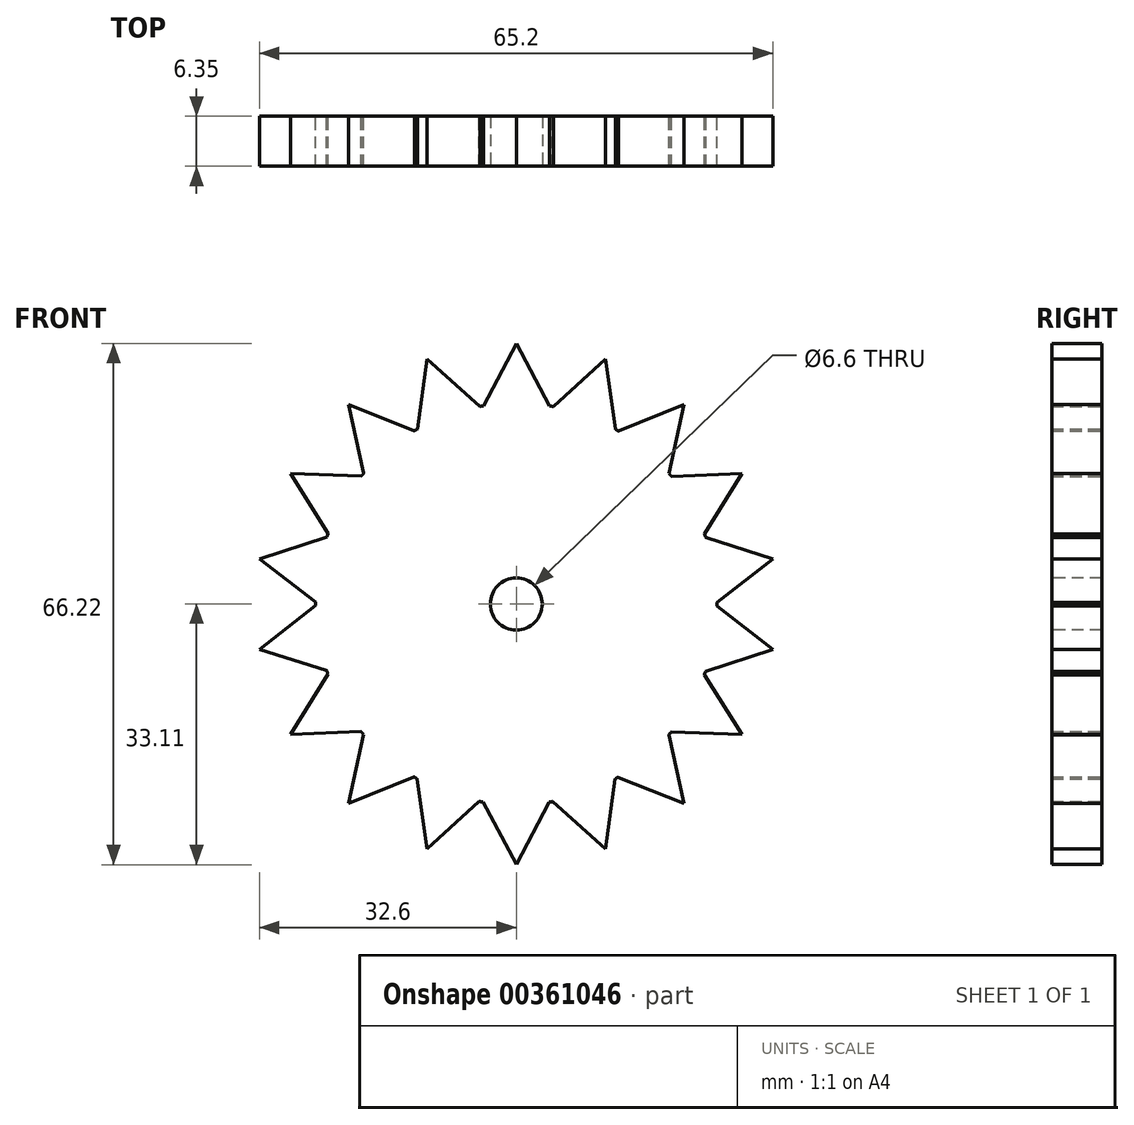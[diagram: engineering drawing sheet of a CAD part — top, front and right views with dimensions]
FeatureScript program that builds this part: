
annotation { "Feature Type Name" : "Feature", "Feature Type Description" : "" }
export const myFeature = defineFeature(function(context is Context, id is Id, definition is map)
    precondition{}
    {
        {
            var Q0;
            Q0=qCreatedBy(makeId("Front.planeOp"),FACE);
            var sketch = newSketch(context, id + "F0", { "sketchPlane" : qUnion([Q0])});
            skCircle(sketch, "E0", {"center": v(0, 0) * mm, "radius": 25.52 * mm});
            skLineSegment(sketch, "E1", {"start": v(-4.16, 25.18) * mm, "end": v(0, 33.1) * mm});
            skLineSegment(sketch, "E2", {"start": v(0, 33.1) * mm, "end": v(4.24, 25.17) * mm});
            skLineSegment(sketch, "E3.1.0", {"start": v(-11.32, 31.11) * mm, "end": v(-4.63, 25.1) * mm});
            skLineSegment(sketch, "E3.1.1", {"start": v(-12.52, 22.24) * mm, "end": v(-11.32, 31.11) * mm});
            skLineSegment(sketch, "E3.2.0", {"start": v(-21.28, 25.36) * mm, "end": v(-12.93, 22) * mm});
            skLineSegment(sketch, "E3.2.1", {"start": v(-19.37, 16.61) * mm, "end": v(-21.28, 25.36) * mm});
            skLineSegment(sketch, "E3.3.0", {"start": v(-28.67, 16.55) * mm, "end": v(-19.68, 16.25) * mm});
            skLineSegment(sketch, "E3.3.1", {"start": v(-23.88, 8.99) * mm, "end": v(-28.67, 16.55) * mm});
            skLineSegment(sketch, "E3.4.0", {"start": v(-32.6, 5.75) * mm, "end": v(-24.05, 8.54) * mm});
            skLineSegment(sketch, "E3.4.1", {"start": v(-25.52, 0.28) * mm, "end": v(-32.6, 5.75) * mm});
            skLineSegment(sketch, "E3.5.0", {"start": v(-32.6, -5.75) * mm, "end": v(-25.52, -0.2) * mm});
            skLineSegment(sketch, "E3.5.1", {"start": v(-24.07, -8.47) * mm, "end": v(-32.6, -5.75) * mm});
            skLineSegment(sketch, "E3.6.0", {"start": v(-28.67, -16.55) * mm, "end": v(-23.91, -8.91) * mm});
            skLineSegment(sketch, "E3.6.1", {"start": v(-19.73, -16.2) * mm, "end": v(-28.67, -16.55) * mm});
            skLineSegment(sketch, "E3.7.0", {"start": v(-21.28, -25.36) * mm, "end": v(-19.42, -16.56) * mm});
            skLineSegment(sketch, "E3.7.1", {"start": v(-13, -21.96) * mm, "end": v(-21.28, -25.36) * mm});
            skLineSegment(sketch, "E3.8.0", {"start": v(-11.32, -31.11) * mm, "end": v(-12.59, -22.2) * mm});
            skLineSegment(sketch, "E3.8.1", {"start": v(-4.7, -25.08) * mm, "end": v(-11.32, -31.11) * mm});
            skLineSegment(sketch, "E3.9.0", {"start": v(0, -33.1) * mm, "end": v(-4.24, -25.17) * mm});
            skLineSegment(sketch, "E3.9.1", {"start": v(4.16, -25.18) * mm, "end": v(0, -33.1) * mm});
            skLineSegment(sketch, "E3.10.0", {"start": v(11.32, -31.11) * mm, "end": v(4.63, -25.1) * mm});
            skLineSegment(sketch, "E3.10.1", {"start": v(12.52, -22.24) * mm, "end": v(11.32, -31.11) * mm});
            skLineSegment(sketch, "E3.11.0", {"start": v(21.28, -25.36) * mm, "end": v(12.93, -22) * mm});
            skLineSegment(sketch, "E3.11.1", {"start": v(19.37, -16.61) * mm, "end": v(21.28, -25.36) * mm});
            skLineSegment(sketch, "E3.12.0", {"start": v(28.67, -16.55) * mm, "end": v(19.68, -16.25) * mm});
            skLineSegment(sketch, "E3.12.1", {"start": v(23.88, -8.99) * mm, "end": v(28.67, -16.55) * mm});
            skLineSegment(sketch, "E3.13.0", {"start": v(32.6, -5.75) * mm, "end": v(24.05, -8.54) * mm});
            skLineSegment(sketch, "E3.13.1", {"start": v(25.52, -0.28) * mm, "end": v(32.6, -5.75) * mm});
            skLineSegment(sketch, "E3.14.0", {"start": v(32.6, 5.75) * mm, "end": v(25.52, 0.2) * mm});
            skLineSegment(sketch, "E3.14.1", {"start": v(24.07, 8.47) * mm, "end": v(32.6, 5.75) * mm});
            skLineSegment(sketch, "E3.15.0", {"start": v(28.67, 16.55) * mm, "end": v(23.91, 8.91) * mm});
            skLineSegment(sketch, "E3.15.1", {"start": v(19.73, 16.2) * mm, "end": v(28.67, 16.55) * mm});
            skLineSegment(sketch, "E3.16.0", {"start": v(21.28, 25.36) * mm, "end": v(19.42, 16.56) * mm});
            skLineSegment(sketch, "E3.16.1", {"start": v(13, 21.96) * mm, "end": v(21.28, 25.36) * mm});
            skLineSegment(sketch, "E3.17.0", {"start": v(11.32, 31.11) * mm, "end": v(12.59, 22.2) * mm});
            skLineSegment(sketch, "E3.17.1", {"start": v(4.7, 25.08) * mm, "end": v(11.32, 31.11) * mm});
            skSolve(sketch);
        }
        {
            var Q0;
            Q0 = qSketchRegion(id + "F0", true);
            extrude(context, id + "F1", {"entities" : qUnion([Q0]), "depth" : 6.35 * mm});
        }
        {
            var Q0;
            Q0=makeQuery(id+"F1.opExtrude","CAP_FACE",FACE,{"disambiguationData":[OSD([sQuery(id+"F0.wireOp",EDGE,"E0"),sQuery(id+"F0.wireOp",EDGE,"E1"),sQuery(id+"F0.wireOp",EDGE,"E2"),sQuery(id+"F0.wireOp",EDGE,"E3.1.0"),sQuery(id+"F0.wireOp",EDGE,"E3.1.1"),sQuery(id+"F0.wireOp",EDGE,"E3.2.0"),sQuery(id+"F0.wireOp",EDGE,"E3.2.1"),sQuery(id+"F0.wireOp",EDGE,"E3.3.0"),sQuery(id+"F0.wireOp",EDGE,"E3.3.1"),sQuery(id+"F0.wireOp",EDGE,"E3.4.0"),sQuery(id+"F0.wireOp",EDGE,"E3.4.1"),sQuery(id+"F0.wireOp",EDGE,"E3.5.0"),sQuery(id+"F0.wireOp",EDGE,"E3.5.1"),sQuery(id+"F0.wireOp",EDGE,"E3.6.0"),sQuery(id+"F0.wireOp",EDGE,"E3.6.1"),sQuery(id+"F0.wireOp",EDGE,"E3.7.0"),sQuery(id+"F0.wireOp",EDGE,"E3.7.1"),sQuery(id+"F0.wireOp",EDGE,"E3.8.0"),sQuery(id+"F0.wireOp",EDGE,"E3.8.1"),sQuery(id+"F0.wireOp",EDGE,"E3.9.0"),sQuery(id+"F0.wireOp",EDGE,"E3.9.1"),sQuery(id+"F0.wireOp",EDGE,"E3.10.0"),sQuery(id+"F0.wireOp",EDGE,"E3.10.1"),sQuery(id+"F0.wireOp",EDGE,"E3.11.0"),sQuery(id+"F0.wireOp",EDGE,"E3.11.1"),sQuery(id+"F0.wireOp",EDGE,"E3.12.0"),sQuery(id+"F0.wireOp",EDGE,"E3.12.1"),sQuery(id+"F0.wireOp",EDGE,"E3.13.0"),sQuery(id+"F0.wireOp",EDGE,"E3.13.1"),sQuery(id+"F0.wireOp",EDGE,"E3.14.0"),sQuery(id+"F0.wireOp",EDGE,"E3.14.1"),sQuery(id+"F0.wireOp",EDGE,"E3.15.0"),sQuery(id+"F0.wireOp",EDGE,"E3.15.1"),sQuery(id+"F0.wireOp",EDGE,"E3.16.0"),sQuery(id+"F0.wireOp",EDGE,"E3.16.1"),sQuery(id+"F0.wireOp",EDGE,"E3.17.0"),sQuery(id+"F0.wireOp",EDGE,"E3.17.1")])],"isStart":false});
            var sketch = newSketch(context, id + "F2", { "sketchPlane" : qUnion([Q0])});
            skCircle(sketch, "E4", {"center": v(0, 0) * mm, "radius": 3.3 * mm});
            skSolve(sketch);
        }
        {
            var Q0;
            Q0 = qSketchRegion(id + "F2", true);
            extrude(context, id + "F3", {"entities" : qUnion([Q0]), "operationType" : NewBodyOperationType.REMOVE, "oppositeDirection" : true, "depth" : 6.35 * mm});
        }
    });
